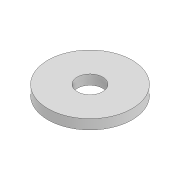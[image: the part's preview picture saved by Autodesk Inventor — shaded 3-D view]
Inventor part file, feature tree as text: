
AUTODESK INVENTOR PART (.ipt)
format: ipt  version: 2022 (Build 260153000, 153)  size: 87,040 bytes
history: native  units: mm
features: extrude x1, sketch x1
ambient origin geometry x8: Origin, YZ Plane, XZ Plane, XY Plane, X Axis, Y Axis, Z Axis, Center Point
bodies: Solid1 (feature_tree)
feature tree (2):
  extrude  "Extrusion1"  Depth=10.0mm
  sketch  "Sketch1"  dims[d0=3.1mm d1=10.0mm d2=4.0mm d3=0.0mm d4=0.2mm d5=12.0mm]
